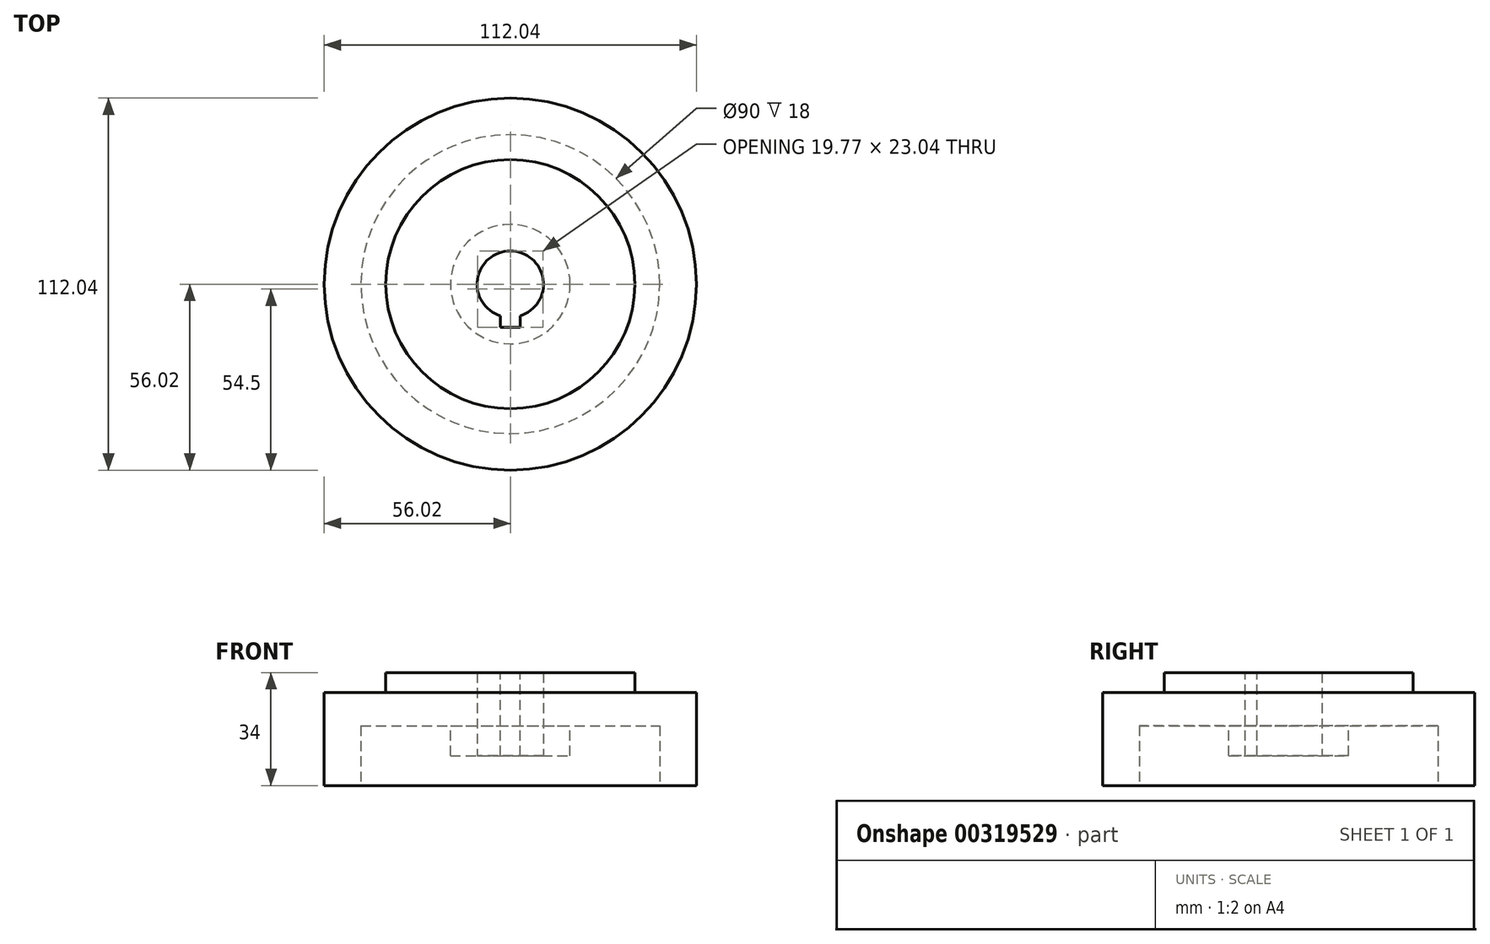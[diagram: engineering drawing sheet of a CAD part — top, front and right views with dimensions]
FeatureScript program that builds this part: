
annotation { "Feature Type Name" : "Feature", "Feature Type Description" : "" }
export const myFeature = defineFeature(function(context is Context, id is Id, definition is map)
    precondition{}
    {
        {
            var Q0;
            Q0=qCreatedBy(makeId("Top.planeOp"),FACE);
            var sketch = newSketch(context, id + "F0", { "sketchPlane" : qUnion([Q0])});
            skCircle(sketch, "E0", {"center": v(0, 0) * mm, "radius": 56.02 * mm});
            skCircle(sketch, "E1", {"center": v(0, 0) * mm, "radius": 10 * mm});
            skSolve(sketch);
        }
        {
            var Q0;
            Q0=makeQuery(id+"F0.imprint","IMPRINT",FACE,{"disambiguationData":[TD([[makeQuery(id+"F0.imprint","IMPRINT",EDGE,{"derivedFrom":sQuery(id+"F0.wireOp",EDGE,"E0")}),1.0]])]});
            extrude(context, id + "F1", {"entities" : qUnion([Q0]), "depth" : 28 * mm});
        }
        {
            var Q0;
            Q0=makeQuery(id+"F1.opExtrude","CAP_FACE",FACE,{"disambiguationData":[OSD([sQuery(id+"F0.wireOp",EDGE,"E0"),sQuery(id+"F0.wireOp",EDGE,"E1")])],"isStart":false});
            var sketch = newSketch(context, id + "F2", { "sketchPlane" : qUnion([Q0])});
            skCircle(sketch, "E2", {"center": v(0, 0) * mm, "radius": 37.5 * mm});
            skSolve(sketch);
        }
        {
            var Q0;
            Q0=makeQuery(id+"F2.imprint","IMPRINT",FACE,{"disambiguationData":[TD([[makeQuery(id+"F2.imprint","IMPRINT",EDGE,{"derivedFrom":sQuery(id+"F2.wireOp",EDGE,"E2")}),1.0]])]});
            extrude(context, id + "F3", {"entities" : qUnion([Q0]), "operationType" : NewBodyOperationType.ADD, "depth" : 6 * mm});
        }
        {
            var Q0;
            Q0=makeQuery(id+"F1.opExtrude","CAP_FACE",FACE,{"disambiguationData":[OSD([sQuery(id+"F0.wireOp",EDGE,"E0"),sQuery(id+"F0.wireOp",EDGE,"E1")])],"isStart":true});
            var sketch = newSketch(context, id + "F4", { "sketchPlane" : qUnion([Q0])});
            skCircle(sketch, "E3", {"center": v(0, 0) * mm, "radius": 45 * mm});
            skSolve(sketch);
        }
        {
            var Q0;
            Q0=makeQuery(id+"F4.imprint","IMPRINT",FACE,{"disambiguationData":[TD([[makeQuery(id+"F4.imprint","IMPRINT",EDGE,{"derivedFrom":sQuery(id+"F4.wireOp",EDGE,"E3")}),1.0]])]});
            extrude(context, id + "F5", {"entities" : qUnion([Q0]), "operationType" : NewBodyOperationType.REMOVE, "oppositeDirection" : true, "depth" : 18 * mm});
        }
        {
            var Q0;
            Q0=makeQuery(id+"F5.boolean.opBoolean","COPY",FACE,{"derivedFrom":makeQuery(id+"F5.opExtrude","CAP_FACE",FACE,{"disambiguationData":[OSD([sQuery(id+"F0.wireOp",EDGE,"E1"),sQuery(id+"F4.wireOp",EDGE,"E3")])],"isStart":false})});
            var sketch = newSketch(context, id + "F6", { "sketchPlane" : qUnion([Q0])});
            skCircle(sketch, "E4", {"center": v(0, 0) * mm, "radius": 18 * mm});
            skSolve(sketch);
        }
        {
            var Q0;
            Q0=makeQuery(id+"F6.imprint","IMPRINT",FACE,{"disambiguationData":[TD([[makeQuery(id+"F6.imprint","IMPRINT",EDGE,{"derivedFrom":sQuery(id+"F6.wireOp",EDGE,"E4")}),1.0]])]});
            extrude(context, id + "F7", {"entities" : qUnion([Q0]), "operationType" : NewBodyOperationType.ADD, "depth" : 9 * mm});
        }
        {
            var Q0;
            Q0=makeQuery(id+"F3.opExtrude","CAP_FACE",FACE,{"disambiguationData":[OSD([sQuery(id+"F0.wireOp",EDGE,"E1"),sQuery(id+"F2.wireOp",EDGE,"E2")])],"isStart":false});
            var sketch = newSketch(context, id + "F8", { "sketchPlane" : qUnion([Q0])});
            skLineSegment(sketch, "E5", {"start": v(-3, -9.54) * mm, "end": v(-3, -13.04) * mm});
            skLineSegment(sketch, "E6", {"start": v(-3, -13.04) * mm, "end": v(3, -13.04) * mm});
            skLineSegment(sketch, "E7", {"start": v(3, -13.04) * mm, "end": v(3, -9.54) * mm});
            skSolve(sketch);
        }
        {
            var Q0;
            {var subQ0=sQuery(id+"F8.wireOp",EDGE,"E5");Q0=makeQuery(id+"F8.imprint","IMPRINT",FACE,{"disambiguationData":[TD([[makeQuery(id+"F8.imprint","IMPRINT",EDGE,{"derivedFrom":subQ0}),1.0]])]});}
            extrude(context, id + "F9", {"entities" : qUnion([Q0]), "operationType" : NewBodyOperationType.REMOVE, "oppositeDirection" : true, "depth" : 25 * mm});
        }
    });
